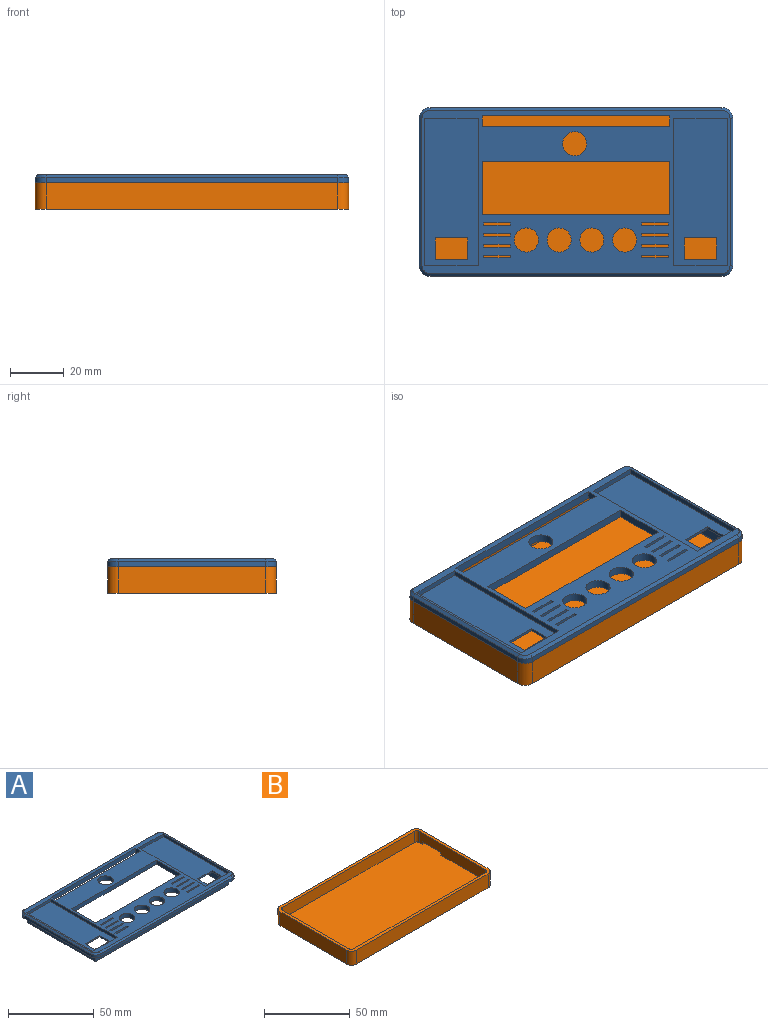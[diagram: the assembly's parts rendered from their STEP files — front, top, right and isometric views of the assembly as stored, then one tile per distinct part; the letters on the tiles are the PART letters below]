
ASSEMBLY  parts=2 mates=1
PART A: 97 faces, bbox 117x63x8 mm
  f0: plane 117x63mm, normal (0,0,-1), area 4667.6mm2, adj f4,f5,f7,f8,f9,f10,f11,f12
  f1: plane 115x61mm, normal (0,0,1), area 2729.2mm2, adj f15,f16,f17,f18,f19,f20,f21,f22
  f2: plane 55x20mm, normal (0,0,1), area 1004mm2, adj f15,f16,f17,f18,f54,f55,f56,f57
  f3: plane 55x20mm, normal (0,0,1), area 1004mm2, adj f19,f20,f21,f22,f50,f51,f52,f53
  f4: plane 6.72x5mm, normal (0,-1,-0.05), area 33mm2, adj f0,f6,f39,f43
  f5: plane 8.26x5mm, normal (0,1,-0.05), area 40.7mm2, adj f0,f6,f35,f43
  f6: plane 110.08x56.08mm, normal (0,0,-1), area 297.4mm2, adj f4,f5,f35,f36,f37,f38,f39,f40
  f7: plane 55x2mm, normal (-1,0,0), area 110mm2, adj f0,f11,f14,f26
  f8: plane 109x2mm, normal (0,-1,0), area 218mm2, adj f0,f11,f12,f23
  f9: plane 55x2mm, normal (1,0,0), area 110mm2, adj f0,f12,f13,f27
  f10: plane 109x2mm, normal (0,1,0), area 218mm2, adj f0,f13,f14,f30
  f11: cylinder r=4mm len=4mm, axis (0,0,1), area 12.6mm2, adj f0,f7,f8,f24
  f12: cylinder r=4mm len=4mm, axis (0,0,-1), area 12.6mm2, adj f0,f8,f9,f25
  f13: cylinder r=4mm len=4mm, axis (0,0,1), area 12.6mm2, adj f0,f9,f10,f29
  f14: cylinder r=4mm len=4mm, axis (0,0,-1), area 12.6mm2, adj f0,f7,f10,f28
  f15: plane 20x2mm, normal (0,-1,0), area 40mm2, adj f1,f2,f16,f18
  f16: plane 55x2mm, normal (1,0,0), area 110mm2, adj f1,f2,f15,f17
  f17: plane 20x2mm, normal (0,1,0), area 40mm2, adj f1,f2,f16,f18
  f18: plane 55x2mm, normal (-1,0,0), area 110mm2, adj f1,f2,f15,f17
  f19: plane 20x2mm, normal (0,-1,0), area 40mm2, adj f1,f3,f20,f22
  f20: plane 55x2mm, normal (1,0,0), area 110mm2, adj f1,f3,f19,f21
  f21: plane 20x2mm, normal (0,1,0), area 40mm2, adj f1,f3,f20,f22
  f22: plane 55x2mm, normal (-1,0,0), area 110mm2, adj f1,f3,f19,f21
  f23: plane 109x1mm, normal (0,-0.71,0.71), area 154.1mm2, adj f1,f8,f24,f25
  f24: cone r=3mm half-angle=45deg, axis (0,0,-1), area 7.8mm2, adj f1,f11,f23,f26
  f25: cone r=3mm half-angle=45deg, axis (0,0,-1), area 7.8mm2, adj f1,f12,f23,f27
  f26: plane 55x1mm, normal (-0.71,0,0.71), area 77.8mm2, adj f1,f7,f24,f28
  f27: plane 55x1mm, normal (0.71,0,0.71), area 77.8mm2, adj f1,f9,f25,f29
  f28: cone r=3mm half-angle=45deg, axis (0,0,-1), area 7.8mm2, adj f1,f14,f26,f30
  f29: cone r=3mm half-angle=45deg, axis (0,0,-1), area 7.8mm2, adj f1,f13,f27,f30
  f30: plane 109x1mm, normal (0,0.71,0.71), area 154.1mm2, adj f1,f10,f28,f29
  f31: plane 70x3mm, normal (0,-1,0), area 210mm2, adj f0,f1,f32,f34
  f32: plane 20x3mm, normal (1,0,0), area 60mm2, adj f0,f1,f31,f33
  f33: plane 70x3mm, normal (0,1,0), area 210mm2, adj f0,f1,f32,f34
  f34: plane 20x3mm, normal (-1,0,0), area 60mm2, adj f0,f1,f31,f33
  f35: plane 56.6x5mm, normal (1,0,-0.05), area 279.4mm2, adj f0,f5,f6,f36,f90,f91
  f36: plane 110.6x5mm, normal (0,-1,-0.05), area 552.4mm2, adj f0,f6,f35,f37
  f37: plane 56.6x5mm, normal (-1,0,-0.05), area 280.7mm2, adj f0,f6,f36,f42,f92
  f38: plane 107.52x5mm, normal (0,1,-0.05), area 537mm2, adj f0,f6,f39,f41
  f39: plane 53.52x5mm, normal (-1,0,-0.05), area 264mm2, adj f0,f4,f6,f38,f90,f91
  f40: plane 6.72x5mm, normal (0,-1,-0.05), area 33mm2, adj f0,f6,f41,f44
  f41: plane 53.55x5.03mm, normal (1,0,-0.05), area 265.3mm2, adj f0,f6,f38,f40,f92
  f42: plane 8.26x5mm, normal (0,1,-0.05), area 40.7mm2, adj f0,f6,f37,f44
  f43: plane 5x1.8mm, normal (-1,0,0), area 7.7mm2, adj f0,f4,f5,f6
  f44: plane 5x1.8mm, normal (1,0,0), area 7.7mm2, adj f0,f6,f40,f42
  f45: cylinder r=4.5mm len=9mm, axis (0,0,1), area 84.8mm2, adj f0,f1
  f46: plane 70x3mm, normal (0,1,0), area 210mm2, adj f0,f1,f47,f49
  f47: plane 4x3mm, normal (-1,0,0), area 12mm2, adj f0,f1,f46,f48
  f48: plane 70x3mm, normal (0,-1,0), area 210mm2, adj f0,f1,f47,f49
  f49: plane 4x3mm, normal (1,0,0), area 12mm2, adj f0,f1,f46,f48
  f50: plane 12x1mm, normal (0,-1,0), area 12mm2, adj f0,f3,f51,f53
  f51: plane 8x1mm, normal (1,0,0), area 8mm2, adj f0,f3,f50,f52
  f52: plane 12x1mm, normal (0,1,0), area 12mm2, adj f0,f3,f51,f53
  f53: plane 8x1mm, normal (-1,0,0), area 8mm2, adj f0,f3,f50,f52
  f54: plane 12x1mm, normal (0,-1,0), area 12mm2, adj f0,f2,f55,f57
  f55: plane 8x1mm, normal (1,0,0), area 8mm2, adj f0,f2,f54,f56
  f56: plane 12x1mm, normal (0,1,0), area 12mm2, adj f0,f2,f55,f57
  f57: plane 8x1mm, normal (-1,0,0), area 8mm2, adj f0,f2,f54,f56
  f58: plane 3x1mm, normal (-1,0,0), area 3mm2, adj f0,f1,f59,f61
  f59: plane 10x3mm, normal (0,-1,0), area 30mm2, adj f0,f1,f58,f60
  f60: plane 3x1mm, normal (1,0,0), area 3mm2, adj f0,f1,f59,f61
  f61: plane 10x3mm, normal (0,1,0), area 30mm2, adj f0,f1,f58,f60
  f62: plane 3x1mm, normal (-1,0,0), area 3mm2, adj f0,f1,f63,f65
  f63: plane 10x3mm, normal (0,-1,0), area 30mm2, adj f0,f1,f62,f64
  f64: plane 3x1mm, normal (1,0,0), area 3mm2, adj f0,f1,f63,f65
  f65: plane 10x3mm, normal (0,1,0), area 30mm2, adj f0,f1,f62,f64
  f66: plane 3x1mm, normal (-1,0,0), area 3mm2, adj f0,f1,f67,f69
  f67: plane 10x3mm, normal (0,-1,0), area 30mm2, adj f0,f1,f66,f68
  f68: plane 3x1mm, normal (1,0,0), area 3mm2, adj f0,f1,f67,f69
  f69: plane 10x3mm, normal (0,1,0), area 30mm2, adj f0,f1,f66,f68
  f70: plane 3x1mm, normal (-1,0,0), area 3mm2, adj f0,f1,f71,f73
  f71: plane 10x3mm, normal (0,-1,0), area 30mm2, adj f0,f1,f70,f72
  f72: plane 3x1mm, normal (1,0,0), area 3mm2, adj f0,f1,f71,f73
  f73: plane 10x3mm, normal (0,1,0), area 30mm2, adj f0,f1,f70,f72
  f74: plane 10x3mm, normal (0,-1,0), area 30mm2, adj f0,f1,f75,f77
  f75: plane 3x1mm, normal (1,0,0), area 3mm2, adj f0,f1,f74,f76
  f76: plane 10x3mm, normal (0,1,0), area 30mm2, adj f0,f1,f75,f77
  f77: plane 3x1mm, normal (-1,0,0), area 3mm2, adj f0,f1,f74,f76
  f78: plane 3x1mm, normal (-1,0,0), area 3mm2, adj f0,f1,f79,f81
  f79: plane 10x3mm, normal (0,-1,0), area 30mm2, adj f0,f1,f78,f80
  f80: plane 3x1mm, normal (1,0,0), area 3mm2, adj f0,f1,f79,f81
  f81: plane 10x3mm, normal (0,1,0), area 30mm2, adj f0,f1,f78,f80
  f82: plane 10x3mm, normal (0,-1,0), area 30mm2, adj f0,f1,f83,f85
  f83: plane 3x1mm, normal (1,0,0), area 3mm2, adj f0,f1,f82,f84
  f84: plane 10x3mm, normal (0,1,0), area 30mm2, adj f0,f1,f83,f85
  f85: plane 3x1mm, normal (-1,0,0), area 3mm2, adj f0,f1,f82,f84
  f86: plane 3x1mm, normal (-1,0,0), area 3mm2, adj f0,f1,f87,f89
  f87: plane 10x3mm, normal (0,-1,0), area 30mm2, adj f0,f1,f86,f88
  f88: plane 3x1mm, normal (1,0,0), area 3mm2, adj f0,f1,f87,f89
  f89: plane 10x3mm, normal (0,1,0), area 30mm2, adj f0,f1,f86,f88
  f90: cylinder r=0.65mm len=1.62mm, axis (1,0,-0.05), area 6.1mm2, adj f35,f39
  f91: cylinder r=0.65mm len=1.62mm, axis (1,0,-0.05), area 6.1mm2, adj f35,f39
  f92: cylinder r=0.65mm len=1.62mm, axis (-1,0,-0.05), area 6.1mm2, adj f37,f41
  f93: cylinder r=4.5mm len=9mm, axis (0,0,1), area 84.8mm2, adj f0,f1
  f94: cylinder r=4.5mm len=9mm, axis (0,0,1), area 84.8mm2, adj f0,f1
  f95: cylinder r=4.5mm len=9mm, axis (0,0,1), area 84.8mm2, adj f0,f1
  f96: cylinder r=4.5mm len=9mm, axis (0,0,1), area 84.8mm2, adj f0,f1
PART B: 22 faces, bbox 117x63x10 mm
  f0: plane 55x10mm, normal (1,0,0), area 520mm2, adj f1,f5,f8,f9,f14,f19,f20,f21
  f1: plane 117x63mm, normal (0,0,1), area 693.7mm2, adj f0,f2,f3,f4,f6,f7,f8,f9
  f2: plane 109x10mm, normal (0,1,0), area 1090mm2, adj f1,f5,f6,f9
  f3: plane 55x10mm, normal (-1,0,0), area 550mm2, adj f1,f5,f6,f7
  f4: plane 109x10mm, normal (0,-1,0), area 1090mm2, adj f1,f5,f7,f8
  f5: plane 117x63mm, normal (0,0,-1), area 7357.3mm2, adj f0,f2,f3,f4,f6,f7,f8,f9
  f6: cylinder r=4mm len=10mm, axis (0,0,-1), area 62.8mm2, adj f1,f2,f3,f5
  f7: cylinder r=4mm len=10mm, axis (0,0,1), area 62.8mm2, adj f1,f3,f4,f5
  f8: cylinder r=4mm len=10mm, axis (0,0,-1), area 62.8mm2, adj f0,f1,f4,f5
  f9: cylinder r=4mm len=10mm, axis (0,0,1), area 62.8mm2, adj f0,f1,f2,f5
  f10: plane 109x8mm, normal (0,-1,0), area 872mm2, adj f1,f14,f15,f18
  f11: plane 55x8mm, normal (1,0,0), area 440mm2, adj f1,f14,f15,f16
  f12: plane 109x8mm, normal (0,1,0), area 872mm2, adj f1,f14,f16,f17
  f13: plane 55x8mm, normal (-1,0,0), area 410mm2, adj f1,f14,f17,f18,f19,f20,f21
  f14: plane 115x59mm, normal (0,0,1), area 6693.6mm2, adj f0,f10,f11,f12,f13,f15,f16,f17
  f15: cylinder r=2mm len=8mm, axis (0,0,-1), area 25.1mm2, adj f1,f10,f11,f14
  f16: cylinder r=2mm len=8mm, axis (0,0,1), area 25.1mm2, adj f1,f11,f12,f14
  f17: cylinder r=2mm len=8mm, axis (0,0,-1), area 25.1mm2, adj f1,f12,f13,f14
  f18: cylinder r=2mm len=8mm, axis (0,0,1), area 25.1mm2, adj f1,f10,f13,f14
  f19: plane 15x2mm, normal (0,0,-1), area 30mm2, adj f0,f13,f20,f21
  f20: plane 2x2mm, normal (0,1,0), area 4mm2, adj f0,f13,f14,f19
  f21: plane 2x2mm, normal (0,-1,0), area 4mm2, adj f0,f13,f14,f19
PLACE A t=(22.57,24.67,7.3)mm
PLACE B t=(20.98,6.13,7.3)mm
MATE planar A.f0 <-> B.f1  axis (0,0,-1) through (30.29,25.97,7.3)mm
